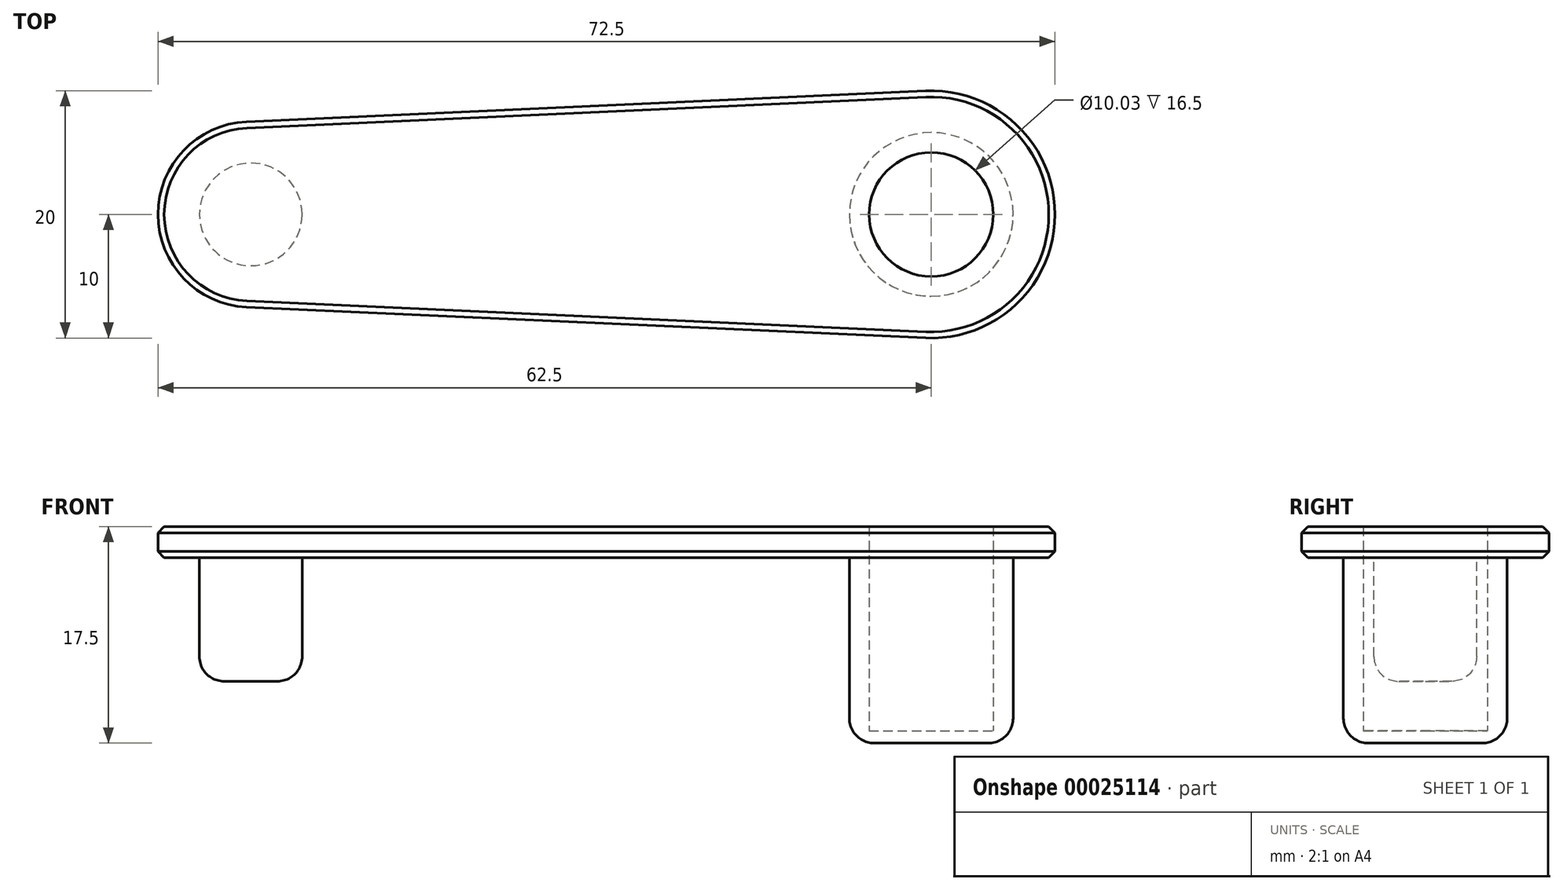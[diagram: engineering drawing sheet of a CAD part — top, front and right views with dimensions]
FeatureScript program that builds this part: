
annotation { "Feature Type Name" : "Feature", "Feature Type Description" : "" }
export const myFeature = defineFeature(function(context is Context, id is Id, definition is map)
    precondition{}
    {
        {
            var Q0;
            Q0=qCreatedBy(makeId("Top.planeOp"),FACE);
            var sketch = newSketch(context, id + "F0", { "sketchPlane" : qUnion([Q0])});
            skCircle(sketch, "E0", {"center": v(0, 0) * mm, "radius": 4.25 * mm, "construction": true});
            skArc(sketch, "E1", {"start": v(-0.34, 7.5) * mm, "mid": v(-7.5, 0) * mm, "end": v(-0.34, -7.5) * mm});
            skLineSegment(sketch, "E2", {"start": v(54.55, 9.99) * mm, "end": v(-0.34, 7.5) * mm});
            skLineSegment(sketch, "E3", {"start": v(54.55, -9.99) * mm, "end": v(-0.34, -7.5) * mm});
            skLineSegment(sketch, "E4", {"start": v(0, 0) * mm, "end": v(55, 0) * mm, "construction": true});
            skArc(sketch, "E5", {"start": v(54.55, -9.99) * mm, "mid": v(65, 0) * mm, "end": v(54.55, 9.99) * mm});
            skCircle(sketch, "E6", {"center": v(55, 0) * mm, "radius": 4.76 * mm, "construction": true});
            skSolve(sketch);
        }
        {
            var Q0;
            Q0 = qSketchRegion(id + "F0", true);
            extrude(context, id + "F1", {"entities" : qUnion([Q0]), "depth" : 2.5 * mm});
        }
        {
            var Q0;
            Q0=makeQuery(id+"F1.opExtrude","CAP_FACE",FACE,{"disambiguationData":[OSD([sQuery(id+"F0.wireOp",EDGE,"bc4cbc08-fc8f-4c5f-a720-618a4acd764b"),sQuery(id+"F0.wireOp",EDGE,"E1"),sQuery(id+"F0.wireOp",EDGE,"E2"),sQuery(id+"F0.wireOp",EDGE,"E3")])],"isStart":true});
            var sketch = newSketch(context, id + "F2", { "sketchPlane" : qUnion([Q0])});
            skCircle(sketch, "E7", {"center": v(0, 0) * mm, "radius": 4.15 * mm});
            skSolve(sketch);
        }
        {
            var Q0;
            Q0 = qSketchRegion(id + "F2", true);
            extrude(context, id + "F3", {"entities" : qUnion([Q0]), "operationType" : NewBodyOperationType.ADD, "depth" : 10 * mm});
        }
        {
            var Q0;
            Q0=makeQuery(id+"F3.opExtrude","CAP_EDGE",EDGE,{"disambiguationData":[OSD([sQuery(id+"F2.wireOp",EDGE,"E7")])],"isStart":false});
            fillet(context, id + "F4", {"entities" : qUnion([Q0]), "radius" : 2 * mm, "tangentPropagation" : true, "allowEdgeOverflow" : false});
        }
        {
            var Q0;
            Q0=makeQuery(id+"F1.opExtrude","CAP_FACE",FACE,{"disambiguationData":[OSD([sQuery(id+"F0.wireOp",EDGE,"E1"),sQuery(id+"F0.wireOp",EDGE,"E2"),sQuery(id+"F0.wireOp",EDGE,"E3"),sQuery(id+"F0.wireOp",EDGE,"E5")])],"isStart":true});
            var sketch = newSketch(context, id + "F5", { "sketchPlane" : qUnion([Q0])});
            skCircle(sketch, "E8", {"center": v(55, 0) * mm, "radius": 5.02 * mm});
            skSolve(sketch);
        }
        {
            var Q0;
            Q0 = qSketchRegion(id + "F5", true);
            extrude(context, id + "F6", {"entities" : qUnion([Q0]), "operationType" : NewBodyOperationType.REMOVE, "endBound" : BoundingType.UP_TO_NEXT, "oppositeDirection" : true, "depth" : 25 * mm});
        }
        {
            var Q0;
            Q0=makeQuery(id+"F1.opExtrude","CAP_FACE",FACE,{"disambiguationData":[OSD([sQuery(id+"F0.wireOp",EDGE,"E1"),sQuery(id+"F0.wireOp",EDGE,"E2"),sQuery(id+"F0.wireOp",EDGE,"E3"),sQuery(id+"F0.wireOp",EDGE,"E5")])],"isStart":true});
            var sketch = newSketch(context, id + "F7", { "sketchPlane" : qUnion([Q0])});
            skCircle(sketch, "E9.0", {"center": v(55, 0) * mm, "radius": 6.62 * mm});
            skSolve(sketch);
        }
        {
            var Q0;
            Q0=makeQuery(id+"F7.imprint","IMPRINT",FACE,{"disambiguationData":[TD([[makeQuery(id+"F7.imprint","IMPRINT",EDGE,{"derivedFrom":sQuery(id+"F7.wireOp",EDGE,"E9.0")}),1.0]])]});
            extrude(context, id + "F8", {"entities" : qUnion([Q0]), "operationType" : NewBodyOperationType.ADD, "depth" : 15 * mm});
        }
        {
            var Q0;
            Q0=makeQuery(id+"F8.opExtrude","CAP_FACE",FACE,{"disambiguationData":[OSD([sQuery(id+"F5.wireOp",EDGE,"E8"),sQuery(id+"F7.wireOp",EDGE,"E9.0")])],"isStart":false});
            var sketch = newSketch(context, id + "F9", { "sketchPlane" : qUnion([Q0])});
            skCircle(sketch, "E10", {"center": v(55, 0) * mm, "radius": 5.02 * mm});
            skSolve(sketch);
        }
        {
            var Q0;
            Q0 = qSketchRegion(id + "F9", true);
            extrude(context, id + "F10", {"entities" : qUnion([Q0]), "operationType" : NewBodyOperationType.ADD, "oppositeDirection" : true, "depth" : 1 * mm});
        }
        {
            var Q0;
            Q0=makeQuery(id+"F1.opExtrude","CAP_EDGE",EDGE,{"disambiguationData":[OSD([sQuery(id+"F0.wireOp",EDGE,"E2")])],"isStart":false});
            var Q1;
            Q1=makeQuery(id+"F6.boolean.opBoolean","COPY",EDGE,{"derivedFrom":makeQuery(id+"F6.opExtrude","CAP_EDGE",EDGE,{"disambiguationData":[OSD([sQuery(id+"F5.wireOp",EDGE,"E8")])],"isStart":false})});
            var Q2;
            Q2=makeQuery(id+"F8.opExtrude","CAP_EDGE",EDGE,{"disambiguationData":[OSD([sQuery(id+"F7.wireOp",EDGE,"E9.0")])],"isStart":true});
            var Q3;
            Q3=makeQuery(id+"F3.opExtrude","CAP_EDGE",EDGE,{"disambiguationData":[OSD([sQuery(id+"F2.wireOp",EDGE,"E7")])],"isStart":true});
            var Q4;
            Q4=makeQuery(id+"F10.opExtrude","CAP_EDGE",EDGE,{"disambiguationData":[OSD([sQuery(id+"F9.wireOp",EDGE,"E10")])],"isStart":false});
            var Q5;
            Q5=makeQuery(id+"F1.opExtrude","CAP_EDGE",EDGE,{"disambiguationData":[OSD([sQuery(id+"F0.wireOp",EDGE,"E2")])],"isStart":true});
            chamfer(context, id + "F11", {"entities" : qUnion([Q0, Q1, Q2, Q3, Q4, Q5]), "width" : .5 * mm, "tangentPropagation" : true});
        }
        {
            var Q0;
            Q0=makeQuery(id+"F8.opExtrude","CAP_EDGE",EDGE,{"disambiguationData":[OSD([sQuery(id+"F7.wireOp",EDGE,"E9.0")])],"isStart":false});
            fillet(context, id + "F12", {"entities" : qUnion([Q0]), "radius" : 2 * mm, "tangentPropagation" : true, "allowEdgeOverflow" : false});
        }
    });
